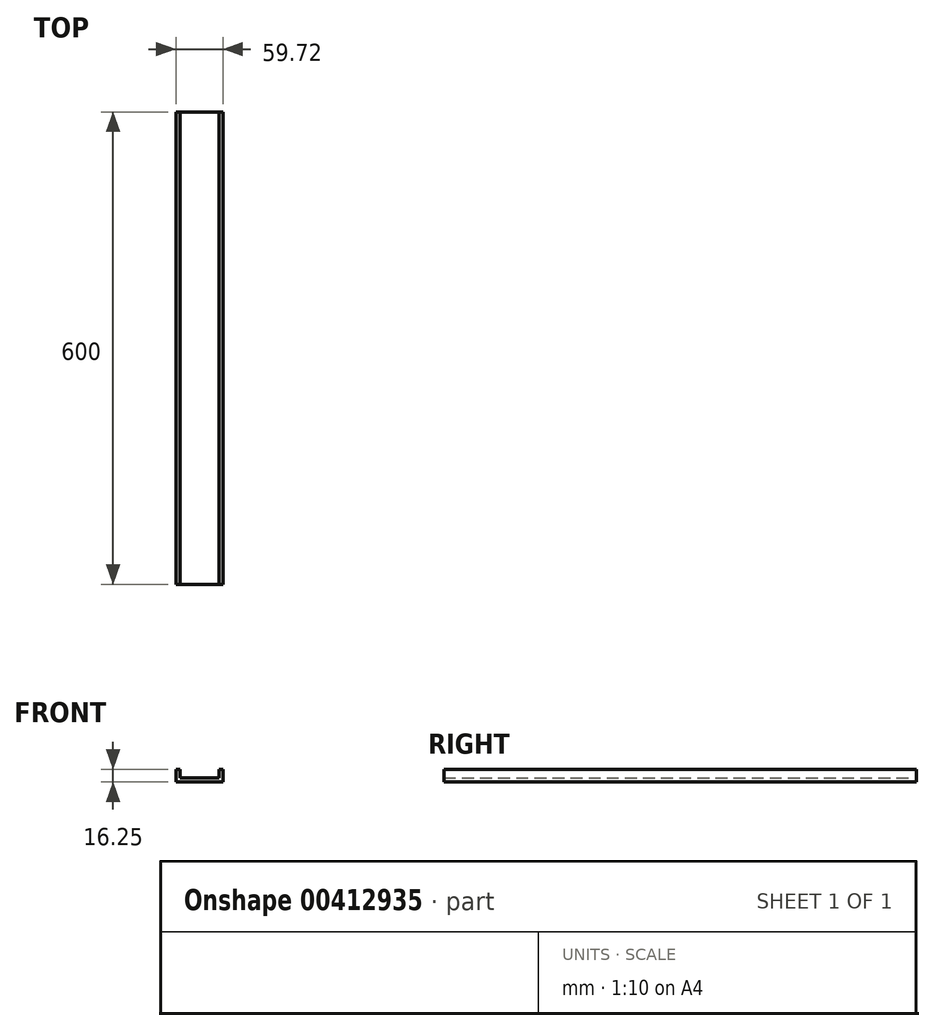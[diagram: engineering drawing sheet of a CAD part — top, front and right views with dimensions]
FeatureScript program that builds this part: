
annotation { "Feature Type Name" : "Feature", "Feature Type Description" : "" }
export const myFeature = defineFeature(function(context is Context, id is Id, definition is map)
    precondition{}
    {
        {
            var Q0;
            Q0=qCreatedBy(makeId("Front.planeOp"),FACE);
            var sketch = newSketch(context, id + "F0", { "sketchPlane" : qUnion([Q0])});
            skLineSegment(sketch, "E0", {"start": v(-24.86, 0) * mm, "end": v(-24.86, -11.25) * mm});
            skLineSegment(sketch, "E1", {"start": v(-24.86, -11.25) * mm, "end": v(0, -11.25) * mm});
            skLineSegment(sketch, "E2", {"start": v(0, -11.25) * mm, "end": v(0, -16.25) * mm});
            skLineSegment(sketch, "E3", {"start": v(0, -16.25) * mm, "end": v(-29.86, -16.25) * mm});
            skLineSegment(sketch, "E4", {"start": v(-29.86, -16.25) * mm, "end": v(-29.86, 0) * mm});
            skLineSegment(sketch, "E5", {"start": v(-29.86, 0) * mm, "end": v(-24.86, 0) * mm});
            skLineSegment(sketch, "E6.MirrorCS", {"start": v(24.86, -11.25) * mm, "end": v(0, -11.25) * mm});
            skLineSegment(sketch, "E7.MirrorCS", {"start": v(0, -16.25) * mm, "end": v(29.86, -16.25) * mm});
            skLineSegment(sketch, "E8.MirrorCS", {"start": v(24.86, 0) * mm, "end": v(24.86, -11.25) * mm});
            skLineSegment(sketch, "E9.MirrorCS", {"start": v(29.86, -16.25) * mm, "end": v(29.86, 0) * mm});
            skLineSegment(sketch, "E10.MirrorCS", {"start": v(29.86, 0) * mm, "end": v(24.86, 0) * mm});
            skSolve(sketch);
        }
        {
            var Q0;
            Q0 = qSketchRegion(id + "F0", true);
            extrude(context, id + "F1", {"entities" : qUnion([Q0]), "depth" : 600 * mm});
        }
    });
